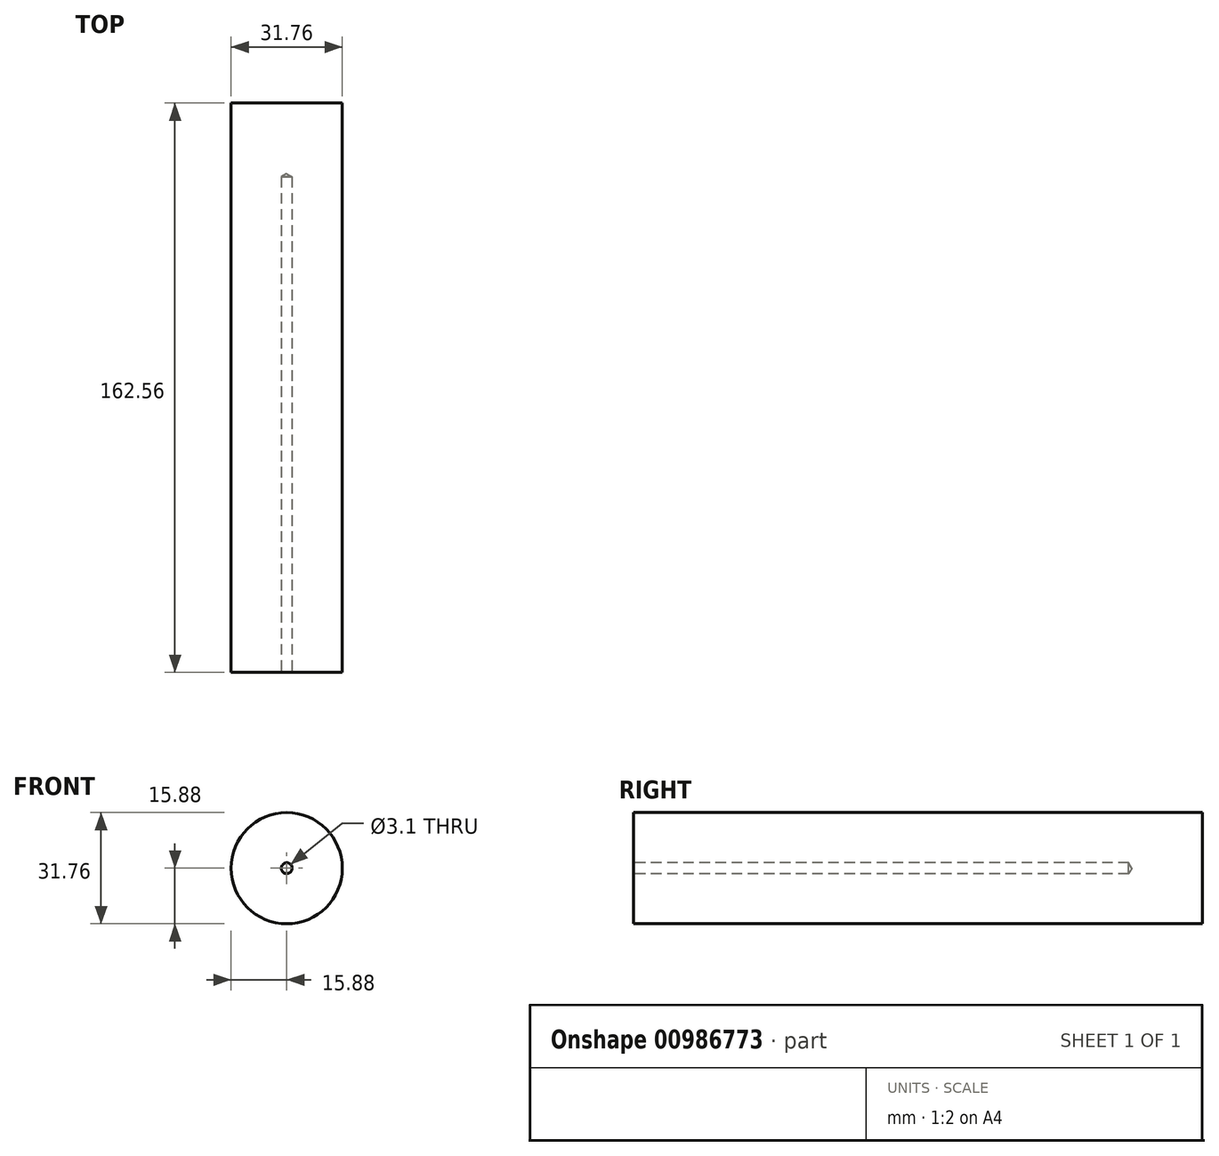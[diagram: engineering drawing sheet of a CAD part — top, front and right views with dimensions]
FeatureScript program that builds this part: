
annotation { "Feature Type Name" : "Feature", "Feature Type Description" : "" }
export const myFeature = defineFeature(function(context is Context, id is Id, definition is map)
    precondition{}
    {
        {
            var Q0;
            Q0=qCreatedBy(makeId("Front.planeOp"),FACE);
            var sketch = newSketch(context, id + "F0", { "sketchPlane" : qUnion([Q0])});
            skCircle(sketch, "E0", {"center": v(0, 0) * mm, "radius": 15.88 * mm});
            skSolve(sketch);
        }
        {
            var Q0;
            Q0=makeQuery(id+"F0.imprint","IMPRINT",FACE,{"disambiguationData":[TD([[makeQuery(id+"F0.imprint","IMPRINT",EDGE,{"derivedFrom":sQuery(id+"F0.wireOp",EDGE,"E0")}),1.0]])]});
            extrude(context, id + "F1", {"entities" : qUnion([Q0]), "oppositeDirection" : true, "depth" : 162.56 * mm, "offsetDistance" : 25.4 * mm});
        }
        {
            var Q0;
            Q0=qCreatedBy(makeId("Front.planeOp"),FACE);
            var sketch = newSketch(context, id + "F2", { "sketchPlane" : qUnion([Q0])});
            skCircle(sketch, "E1", {"center": v(0, 0) * mm, "radius": 1.55 * mm});
            skSolve(sketch);
        }
        {
            var Q0;
            Q0=makeQuery(id+"F2.imprint","IMPRINT",FACE,{"disambiguationData":[TD([[makeQuery(id+"F2.imprint","IMPRINT",EDGE,{"derivedFrom":sQuery(id+"F2.wireOp",EDGE,"E1")}),1.0]])]});
            extrude(context, id + "F3", {"entities" : qUnion([Q0]), "operationType" : NewBodyOperationType.REMOVE, "oppositeDirection" : true, "depth" : 142.37 * mm, "offsetDistance" : 25.4 * mm});
        }
        {
            var Q0;
            Q0=makeQuery(id+"F3.boolean.opBoolean","COPY",EDGE,{"derivedFrom":makeQuery(id+"F3.opExtrude","CAP_EDGE",EDGE,{"disambiguationData":[OSD([sQuery(id+"F2.wireOp",EDGE,"E1")])],"isStart":false})});
            chamfer(context, id + "F4", {"entities" : qUnion([Q0]), "chamferType" : ChamferType.OFFSET_ANGLE, "width" : 1.55 * mm, "oppositeDirection" : false, "angle" : 30 * degree, "tangentPropagation" : true});
        }
    });
